# Revit family: 44289
name_source: partatom
category: Lighting Fixtures
revit_build: Autodesk Revit 2018 (Build: 20170223_1515(x64)
units: mm (PartAtom-declared; Revit-internal decimal feet)

## family parameters
Cut with Voids When Loaded = No
Host = Face
Light Source = Yes
OmniClass Number = 23.80.70.11.17
OmniClass Title = Specialized Lighting by Location or Use
Part Type = Normal
Room Calculation Point = No
Round Connector Dimension = Use Diameter
Shared = No

## types (1)
- 0044289 RUBICO LED 1200 HE 4K DALI EMPRO
    Accessory Material = Steel_Sylvania_Rubico LED_White_RAL 9016
    Ambient temperature for maximum luminous flux (°C) = 25
    Apparent Load = 30 VA
    Assembly Code = D5020200
    Body Material = Steel_Sylvania_Rubico LED_White_RAL 9016
    CRI(Ra) = >80
    Catalog Number = 0044336 RUBICO 300*1200 DALI E3 LED 4000 G2
    Color Filter = 16777215
    Cutout Length = 270 mm  [stored 0.885827 ft]
    Cutout Width = 1170 mm  [stored 3.83858 ft]
    Default Elevation = 0 mm  [stored 0 ft]
    Description = Direct and Indirect light distribution. 31W - 46W LED recessed luminaire. Rubico LED Gen 2 is perfect for Office circulation areas, Corridors . Available with Micro Prismatic Optic (MPO) with satin side diffuser. Available in recessed (600x600 and 1200x300) . Rubico LED Gen 2 delivers high output up to 3,656lm (luminaire lumen output on 4,000K version). Rana LED delivers high efficiency up to 84lm/W (total system efficiency). Available in warm white (3,000K) and neutral white (4,000K). Energy efficient electronic gear including DALI and 3 hour emergency versions as standard. Long lifetime: 50,000 hours life at 70% of the original output L70. Less maintenance is required due to the long lifetime of 50,000hrs. Energy Class: A++, A+, A. LED technology provides an energy efficient solution with reduced maintenance costs. Comes complete with safety cable. Complete with protective film and quick connector for easy installation
    Diffuser 1 Material = Steel_Sylvania_Rubico LED_White_RAL 9016
    Diffuser 2 Material = Polycarbonate_Sylvania_Rubico LED_Clear
    Diffuser Width = 60 mm  [stored 0.19685 ft]
    Dimming Lamp Color Temperature Shift = <None>
    Drive Current = 700mA
    Electrical Protection = CLASS1
    Emit Shape Visible in Rendering = No
    Emit from Rectangle Length = 1166 mm  [stored 3.82546 ft]
    Emit from Rectangle Width = 266 mm  [stored 0.872703 ft]
    Energy Class = A++, A+, A
    Glare Control = 19>
    Glow Wire Test = 850 °C
    Height = 75 mm
    Housing Material = Steel_Sylvania_Rubico LED_White_RAL 9016
    IK Rating = IK07
    IP Rating = IP20
    LOR = 1
    Length = 296 mm  [stored 0.971129 ft]
    Life = 50 000h
    Model = RUBICO LED 1200x300 HE 4K DALI EMPRO
    Photometric Web File = 0044289.ies
    Product Family = RUBICO LED - DALI DIMMABLE & EMERGENCY 3 HOUR
    Product Page URL = http://www.sylvania-lighting.com
    Reflector Material = Steel_Sylvania_Rubico LED_White_RAL 9016
    Tilt Angle = -90.00°
    URL = 0
    Voltage = 230 V
    Voltage Comments = UNI ( Universal Voltage; 230-240 Volt )
    Weight = 4.6 kg
    Width = 1196 mm  [stored 3.92388 ft]

note: [stored X ft] marks values corroborated as IEEE doubles in the binary element streams (Revit-internal decimal feet)

## geometry (parser evidence)
native form markers: Sweep x3
no freeform markers — native parametric forms only
